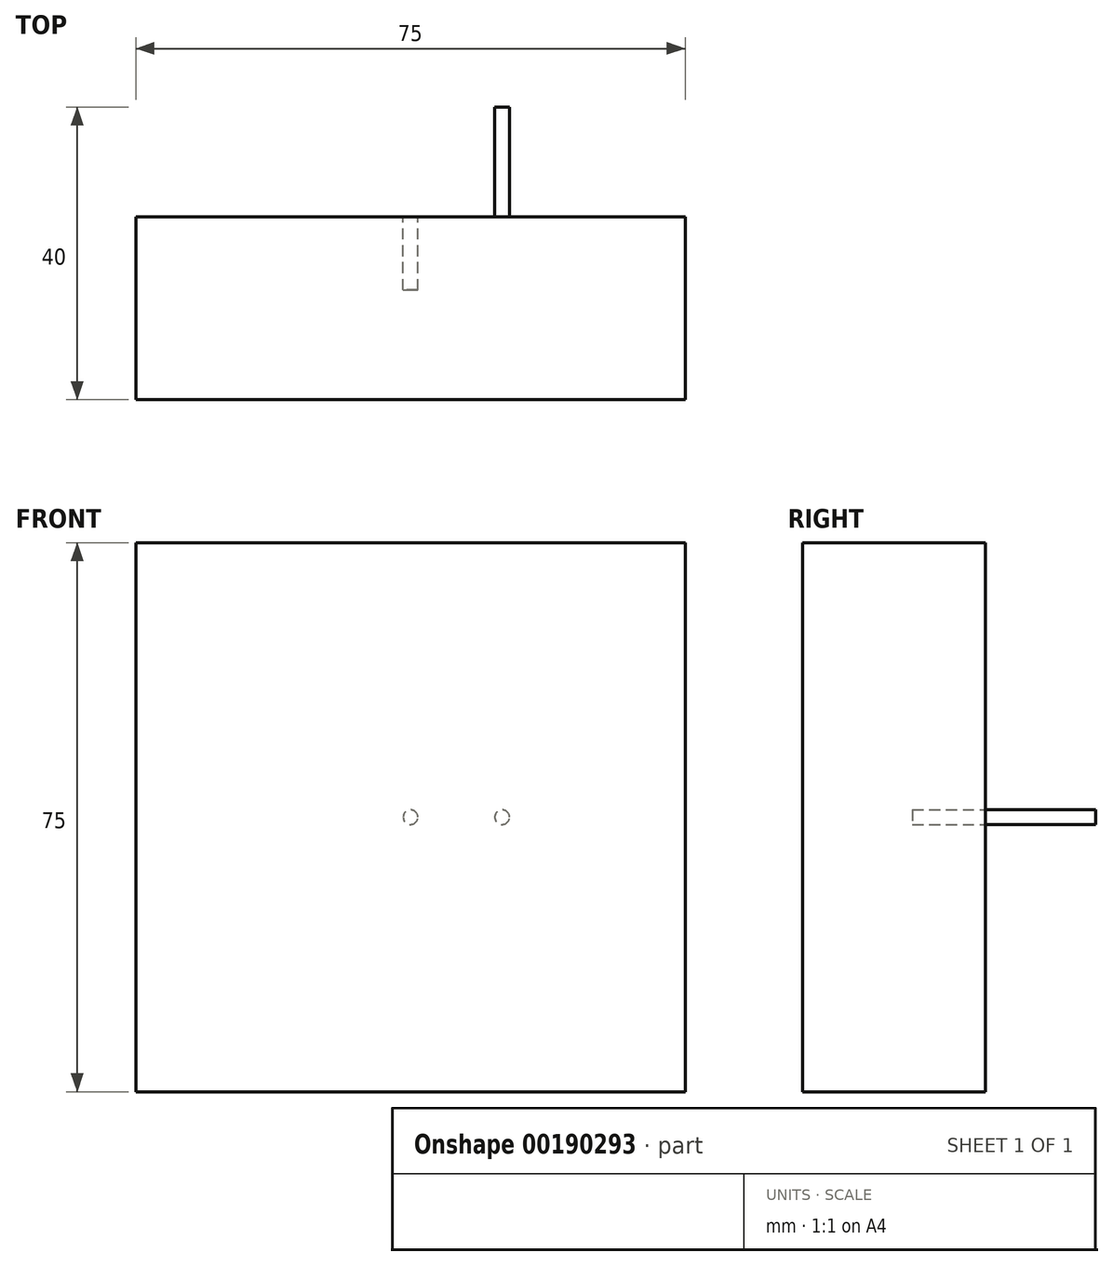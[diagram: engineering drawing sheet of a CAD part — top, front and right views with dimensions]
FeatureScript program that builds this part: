
annotation { "Feature Type Name" : "Feature", "Feature Type Description" : "" }
export const myFeature = defineFeature(function(context is Context, id is Id, definition is map)
    precondition{}
    {
        {
            var Q0;
            Q0=qCreatedBy(makeId("Front.planeOp"),FACE);
            var sketch = newSketch(context, id + "F0", { "sketchPlane" : qUnion([Q0])});
            skLineSegment(sketch, "E0.bottom", {"start": v(37.5, -37.5) * mm, "end": v(-37.5, -37.5) * mm});
            skLineSegment(sketch, "E0.top", {"start": v(37.5, 37.5) * mm, "end": v(-37.5, 37.5) * mm});
            skLineSegment(sketch, "E0.left", {"start": v(37.5, -37.5) * mm, "end": v(37.5, 37.5) * mm});
            skLineSegment(sketch, "E0.right", {"start": v(-37.5, -37.5) * mm, "end": v(-37.5, 37.5) * mm});
            skPoint(sketch, "E0.middle", {"position": v(0, 0) * mm});
            skSolve(sketch);
        }
        {
            var Q0;
            Q0 = qSketchRegion(id + "F0", true);
            extrude(context, id + "F1", {"entities" : qUnion([Q0]), "depth" : 25 * mm});
        }
        {
            var Q0;
            Q0=makeQuery(id+"F1.opExtrude","CAP_FACE",FACE,{"disambiguationData":[OSD([sQuery(id+"F0.wireOp",EDGE,"E0.bottom"),sQuery(id+"F0.wireOp",EDGE,"E0.top"),sQuery(id+"F0.wireOp",EDGE,"E0.left"),sQuery(id+"F0.wireOp",EDGE,"E0.right")])],"isStart":true});
            var sketch = newSketch(context, id + "F2", { "sketchPlane" : qUnion([Q0])});
            skCircle(sketch, "E1", {"center": v(0, 0) * mm, "radius": 1 * mm});
            skSolve(sketch);
        }
        {
            var Q0;
            Q0 = qSketchRegion(id + "F2", true);
            extrude(context, id + "F3", {"entities" : qUnion([Q0]), "operationType" : NewBodyOperationType.REMOVE, "oppositeDirection" : true, "depth" : 10 * mm});
        }
        {
            var Q0;
            Q0=makeQuery(id+"F1.opExtrude","CAP_FACE",FACE,{"disambiguationData":[OSD([sQuery(id+"F0.wireOp",EDGE,"E0.bottom"),sQuery(id+"F0.wireOp",EDGE,"E0.top"),sQuery(id+"F0.wireOp",EDGE,"E0.left"),sQuery(id+"F0.wireOp",EDGE,"E0.right")])],"isStart":true});
            var sketch = newSketch(context, id + "F4", { "sketchPlane" : qUnion([Q0])});
            skCircle(sketch, "E2", {"center": v(-12.5, 0) * mm, "radius": 1 * mm});
            skSolve(sketch);
        }
        {
            var Q0;
            Q0 = qSketchRegion(id + "F4", true);
            extrude(context, id + "F5", {"entities" : qUnion([Q0]), "operationType" : NewBodyOperationType.ADD, "depth" : 15 * mm});
        }
    });
